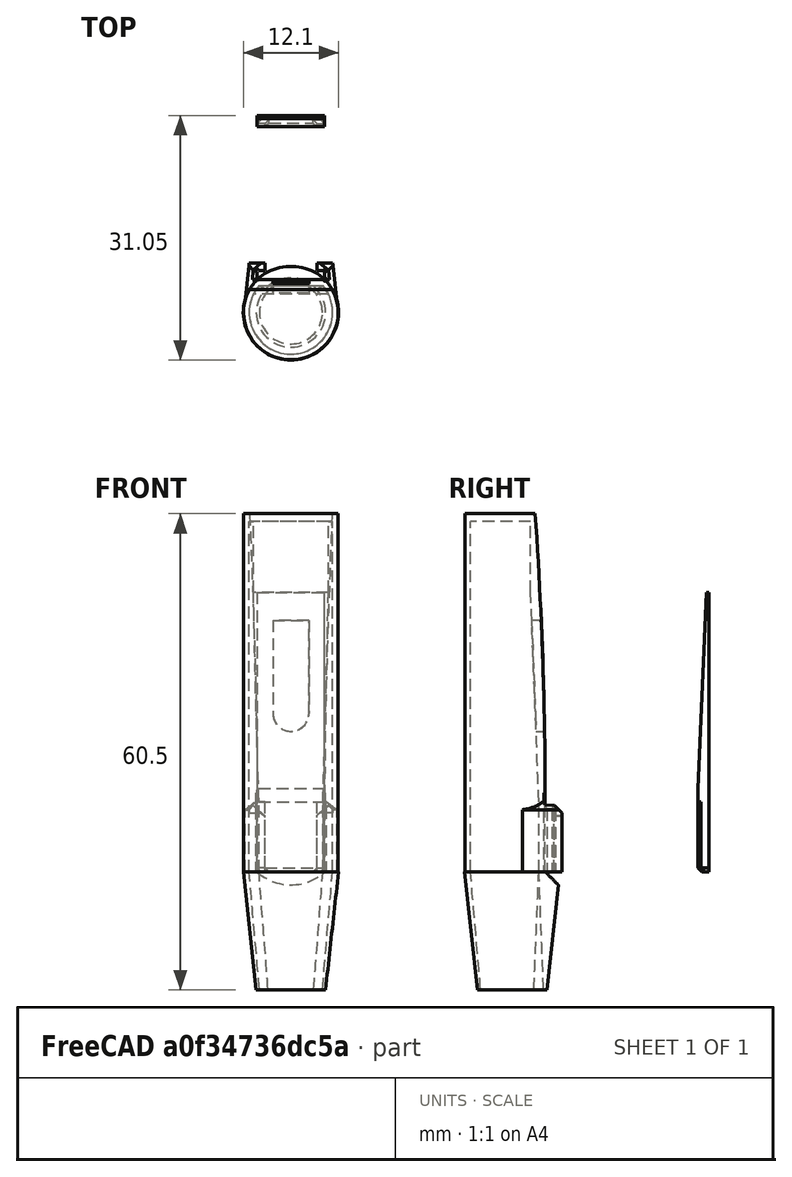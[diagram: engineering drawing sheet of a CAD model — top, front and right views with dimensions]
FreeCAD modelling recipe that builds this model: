
FCSTD DOCUMENT  (FreeCAD 1.0R38641 +678 (Git))
Label: stroik1-D-leaf_PLA
License: All rights reserved
LicenseURL: https://en.wikipedia.org/wiki/All_rights_reserved
objects: Sketcher::SketchObject×17, PartDesign::Pocket×10, PartDesign::Pad×4, PartDesign::Chamfer×3, App::VarSet×2, PartDesign::Body×2, Part::FeaturePython×1, PartDesign::FeatureBase×1, PartDesign::Mirrored×1, PartDesign::Plane×1, PartDesign::AdditiveLoft×1, PartDesign::ShapeBinder×1, Mesh::Feature×1
note: 97 computed .brp shape members not serialized (recipe doc carries the construction recipe); baked Part::Feature solids carry a one-line shape summary decoded from their .brp

FEATURE [Part::FeaturePython] Tube  # WARN: FeaturePython — macro-defined, semantics opaque (R4)
  AttacherType = Attacher::AttachEngine3D
  Height = 35.5
  InnerRadius = 5.3
  OuterRadius = 6
  Placement = pos=(0,0,0) rot=(0,1,0;1.5708rad)
  expr: Height = VarSet.leaf_len
  expr: InnerRadius = VarSet.d_inner
  expr: OuterRadius = VarSet.d_outer
FEATURE [PartDesign::FeatureBase] BaseFeature
  BaseFeature = -> Tube
  Suppressed = false
FEATURE [App::VarSet] VarSet
  d_inner = 5.3
  d_outer = 6
  d_outer_plug = 6.05
  leaf_end_thickness = 0.19
  leaf_gap = 1.85
  leaf_len = 35.5
  leaf_start_thickness = 1.42
  plug_inner_start = 4
  plug_len = 15
  plug_outer_start = 4.4
FEATURE [Sketcher::SketchObject] Sketch
  ArcFitTolerance = 1e-06
  AttachmentSupport = -> [YZ_Plane]
  ExternalGeometry = -> [BaseFeature]
  FullyConstrained = true
  MakeInternals = false
  MapMode = 5
  Placement = pos=(0,0,0) rot=(0.57735,0.57735,0.57735;2.0944rad)
  expr: Constraints[14] = VarSet.leaf_len / 4
  expr: Constraints[8] = VarSet.d_outer * 0.3
  sketch-geometry (6):
    g0: LineSegment StartX=6 StartY=35.5 StartZ=0 EndX=4.2 EndY=35.5 EndZ=0
    g1: LineSegment StartX=4.2 StartY=0 StartZ=0 EndX=6 EndY=0 EndZ=0
    g2: LineSegment StartX=6 StartY=0 StartZ=0 EndX=6 EndY=8.875 EndZ=0
    g3: LineSegment StartX=6 StartY=8.875 StartZ=0 EndX=6 EndY=35.5 EndZ=0
    g4: LineSegment StartX=4.2 StartY=35.5 StartZ=0 EndX=4.2 EndY=8.875 EndZ=0
    g5: LineSegment StartX=4.2 StartY=8.875 StartZ=0 EndX=4.2 EndY=0 EndZ=0
  constraints (17):
    c: Coincident(g0,g4)
    c: Coincident(g5,g1)
    c: Coincident(g1,g2)
    c: Coincident(g3,g0)
    c: Horizontal(g0)
    c: Horizontal(g1)
    c: Coincident(g0,g-3)
    c: PointOnObject(g5,g-4)
    c: DistanceX(g5,g1) = 1.8
    c: Coincident(g2,g3)
    c: Vertical(g2)
    c: Vertical(g3)
    c: Coincident(g4,g5)
    c: Vertical(g5)
    c: DistanceY(g2,g2) = 8.875
    c: Horizontal(g2,g4)
    c: Vertical(g4)
FEATURE [Sketcher::SketchObject] Sketch001
  ArcFitTolerance = 1e-06
  AttachmentSupport = -> [YZ_Plane]
  ExternalGeometry = -> [Sketch]
  FullyConstrained = true
  MakeInternals = false
  MapMode = 5
  Placement = pos=(0,0,0) rot=(0.57735,0.57735,0.57735;2.0944rad)
  expr: Constraints[12] = 0.8
  expr: Constraints[13] = VarSet.leaf_gap
  sketch-geometry (6):
    g0: LineSegment StartX=4.2 StartY=0 StartZ=0 EndX=3.4 EndY=0 EndZ=0
    g1: LineSegment StartX=3.4 StartY=0 StartZ=0 EndX=3.4 EndY=8.875 EndZ=0
    g2: LineSegment StartX=3.4 StartY=8.875 StartZ=0 EndX=2.35 EndY=35.5 EndZ=0
    g3: LineSegment StartX=2.35 StartY=35.5 StartZ=0 EndX=4.2 EndY=35.5 EndZ=0
    g4: LineSegment StartX=4.2 StartY=35.5 StartZ=0 EndX=4.2 EndY=8.875 EndZ=0
    g5: LineSegment StartX=4.2 StartY=8.875 StartZ=0 EndX=4.2 EndY=0 EndZ=0
  constraints (15):
    c: Coincident(g-4,g0)
    c: PointOnObject(g0,g-1)
    c: Coincident(g0,g1)
    c: Vertical(g1)
    c: Coincident(g1,g2)
    c: Coincident(g2,g3)
    c: Coincident(g3,g-3)
    c: Horizontal(g3)
    c: Coincident(g3,g4)
    c: Coincident(g4,g-4)
    c: Coincident(g4,g5)
    c: Coincident(g5,g0)
    c: DistanceX(g1,g4) = 0.8
    c: DistanceX(g2,g3) = 1.85
    c: Horizontal(g1,g4)
FEATURE [PartDesign::Pocket] Pocket  label="1 ścięcie"
  BaseFeature = -> BaseFeature
  Direction = (-1,0,0)
  Length = 5
  Length2 = 5
  Midplane = true
  Profile = -> Sketch
  ReferenceAxis = -> Sketch [N_Axis]
  Refine = true
  Suppressed = false
  Type = 1
FEATURE [PartDesign::Pad] Pad  label="uzupełnienie"
  AlongSketchNormal = false
  BaseFeature = -> Pocket
  Direction = (1,0,0)
  Length = 13
  Length2 = 10
  Midplane = true
  Profile = -> Sketch001
  ReferenceAxis = -> Sketch001 [N_Axis]
  Refine = true
  Suppressed = false
  Type = 1
  UpToShape = -> [Pocket]
FEATURE [PartDesign::Mirrored] Mirrored
  BaseFeature = -> Pad
  MirrorPlane = -> YZ_Plane
  Originals = -> [Pad]
  Refine = true
  Suppressed = false
  TransformMode = 0
FEATURE [Sketcher::SketchObject] Sketch002
  ArcFitTolerance = 1e-06
  AttachmentSupport = -> [Mirrored]
  ExternalGeometry = -> [Mirrored]
  FullyConstrained = true
  MakeInternals = false
  MapMode = 5
  Placement = pos=(0,4.2,0) rot=(0,0.707107,0.707107;3.14159rad)
  expr: Constraints[11] = VarSet.d_outer / 3
  expr: Constraints[8] = VarSet.leaf_len / 10
  expr: Constraints[9] = VarSet.leaf_len / 3
  sketch-geometry (4):
    g0: LineSegment StartX=2.28486 StartY=20.1167 StartZ=0 EndX=2.28486 EndY=31.95 EndZ=0
    g1: LineSegment StartX=2.28486 StartY=31.95 StartZ=0 EndX=-2.28486 EndY=31.95 EndZ=0
    g2: LineSegment StartX=-2.28486 StartY=31.95 StartZ=0 EndX=-2.28486 EndY=20.1167 EndZ=0
    g3: ArcOfCircle CenterX=0 CenterY=20.1167 CenterZ=0 NormalX=0 NormalY=0 NormalZ=1 AngleXU=0 Radius=2.28486 StartAngle=3.14159 EndAngle=6.28319
  constraints (12):
    c: Coincident(g0,g1)
    c: Coincident(g1,g2)
    c: Coincident(g3,g2)
    c: Coincident(g3,g0)
    c: PointOnObject(g3,g-2)
    c: Horizontal(g0,g2)
    c: Horizontal(g2,g3)
    c: Symmetric(g0,g1,g-2)
    c: DistanceY(g1,g-7) = 3.55
    c: DistanceY(g3,g1) = 11.8333
    c: Vertical(g1,g2)
    c: DistanceX(g0,g-6) = 2
FEATURE [PartDesign::Pocket] Pocket001  label="dziurka"
  BaseFeature = -> Mirrored
  Direction = (0,-1,2e-16)
  Length = 2.65
  Length2 = 5
  Profile = -> Sketch002
  ReferenceAxis = -> Sketch002 [N_Axis]
  Refine = true
  Suppressed = false
  Type = 0
  expr: Length = VarSet.d_inner / 2
FEATURE [Sketcher::SketchObject] Sketch003
  ArcFitTolerance = 1e-06
  AttachmentSupport = -> [Pocket001]
  ExternalGeometry = -> [Pocket001]
  FullyConstrained = true
  MakeInternals = false
  MapMode = 5
  Placement = pos=(0,0,35.5) rot=(0,0,1;0rad)
  sketch-geometry (2):
    g0: ArcOfCircle CenterX=0 CenterY=0 CenterZ=0 NormalX=0 NormalY=0 NormalZ=1 AngleXU=0 Radius=6 StartAngle=2.3662 EndAngle=7.05858
    g1: LineSegment StartX=-4.28486 StartY=4.2 StartZ=0 EndX=4.28486 EndY=4.2 EndZ=0
  constraints (5):
    c: Coincident(g0,g-1)
    c: Coincident(g0,g-4)
    c: Coincident(g1,g0)
    c: Coincident(g1,g0)
    c: Horizontal(g1)
FEATURE [PartDesign::Pad] Pad001  label="zaślepka"
  BaseFeature = -> Pocket001
  Direction = (0,0,1)
  Length = 10
  Length2 = 10
  Profile = -> Sketch003
  ReferenceAxis = -> Sketch003 [N_Axis]
  Refine = true
  Suppressed = false
  Type = 0
FEATURE [Sketcher::SketchObject] Sketch004
  ArcFitTolerance = 1e-06
  AttachmentSupport = -> [Pad001]
  ExternalGeometry = -> [Pad001]
  FullyConstrained = true
  MakeInternals = false
  MapMode = 5
  Placement = pos=(0,0,0) rot=(1,0,0;3.14159rad)
  expr: Constraints[4] = VarSet.d_outer_plug
  expr: Constraints[7] = VarSet.d_inner
  sketch-geometry (3):
    g0: ArcOfCircle CenterX=0 CenterY=0 CenterZ=0 NormalX=0 NormalY=0 NormalZ=1 AngleXU=0 Radius=5.3 StartAngle=5.58672 EndAngle=10.1212
    g1: LineSegment StartX=-4.06571 StartY=-3.4 StartZ=0 EndX=4.06571 EndY=-3.4 EndZ=0
    g2: Circle CenterX=0 CenterY=0 CenterZ=0 NormalX=0 NormalY=0 NormalZ=1 AngleXU=0 Radius=6.05
  constraints (8):
    c: Coincident(g1,g0)
    c: Horizontal(g1)
    c: Coincident(g2,g0)
    c: Coincident(g-1,g0)
    c: Radius(g2) = 6.05
    c: Horizontal(g0,g-6)
    c: Coincident(g1,g0)
    c: Radius(g0) = 5.3
FEATURE [PartDesign::Plane] DatumPlane
  AttachmentOffset = pos=(0,0,15) rot=(0,0,1;0rad)
  AttachmentSupport = -> [Pocket001]
  Length = 60
  MapMode = 5
  Placement = pos=(0,0,-15) rot=(1,0,0;3.14159rad)
  ResizeMode = 0
  Width = 60
  expr: .AttachmentOffset.Base.z = VarSet.plug_len
FEATURE [Sketcher::SketchObject] Sketch005
  ArcFitTolerance = 1e-06
  AttachmentSupport = -> [DatumPlane]
  ExternalGeometry = -> [Sketch004,Pad001]
  FullyConstrained = true
  MakeInternals = false
  MapMode = 5
  Placement = pos=(0,0,-15) rot=(1,0,0;3.14159rad)
  expr: Constraints[2] = VarSet.plug_inner_start
  expr: Constraints[3] = VarSet.plug_outer_start
  sketch-geometry (2):
    g0: Circle CenterX=0 CenterY=0 CenterZ=0 NormalX=0 NormalY=0 NormalZ=1 AngleXU=0 Radius=4
    g1: Circle CenterX=0 CenterY=0 CenterZ=0 NormalX=0 NormalY=0 NormalZ=1 AngleXU=0 Radius=4.4
  constraints (4):
    c: Coincident(g0,g-1)
    c: Coincident(g1,g0)
    c: Radius(g0) = 4
    c: Radius(g1) = 4.4
FEATURE [PartDesign::AdditiveLoft] AdditiveLoft  label="dziubek"
  BaseFeature = -> Pad001
  Closed = false
  Profile = -> Sketch005
  Refine = true
  Ruled = false
  Sections = -> [Sketch004]
  Suppressed = false
FEATURE [Sketcher::SketchObject] Sketch006
  ArcFitTolerance = 1e-06
  AttachmentSupport = -> [Pad001]
  ExternalGeometry = -> [Pad001]
  FullyConstrained = false
  MakeInternals = false
  MapMode = 5
  Placement = pos=(0,0,0) rot=(1,0,0;3.14159rad)
  expr: Constraints[24] = 1.1 mm
  sketch-geometry (16):
    g0: LineSegment StartX=4.28486 StartY=-4.2 StartZ=0 EndX=6 EndY=0 EndZ=0
    g1: LineSegment StartX=6 StartY=0 StartZ=0 EndX=5.28986 EndY=-6.3 EndZ=0
    g2: LineSegment StartX=5.28986 StartY=-6.3 StartZ=0 EndX=3.28986 EndY=-6.3 EndZ=0
    g3: LineSegment StartX=3.28986 StartY=-6.3 StartZ=0 EndX=3.28986 EndY=-5.3 EndZ=0
    g4: LineSegment StartX=3.28986 StartY=-5.3 StartZ=0 EndX=4.28986 EndY=-5.3 EndZ=0
    g5: LineSegment StartX=-5.28986 StartY=-6.3 StartZ=0 EndX=-3.28986 EndY=-6.3 EndZ=0
    g6: LineSegment StartX=-6 StartY=0 StartZ=0 EndX=-5.28986 EndY=-6.3 EndZ=0
    g7: LineSegment StartX=-4.28486 StartY=-4.2 StartZ=0 EndX=-6 EndY=0 EndZ=0
    g8: LineSegment StartX=-3.28986 StartY=-5.3 StartZ=0 EndX=-4.28986 EndY=-5.3 EndZ=0
    g9: LineSegment StartX=-3.28986 StartY=-6.3 StartZ=0 EndX=-3.28986 EndY=-5.3 EndZ=0
    g10: LineSegment StartX=4.28986 StartY=-5.3 StartZ=0 EndX=4.28986 EndY=-4.2 EndZ=0
    g11: LineSegment StartX=-4.28986 StartY=-5.3 StartZ=0 EndX=-4.28986 EndY=-4.2 EndZ=0
    g12: LineSegment StartX=4.28986 StartY=-4.2 StartZ=0 EndX=4.28717 EndY=-4.19654 EndZ=0
    g13: LineSegment StartX=4.28717 StartY=-4.19654 StartZ=0 EndX=4.28486 EndY=-4.2 EndZ=0
    g14: LineSegment StartX=-4.28986 StartY=-4.2 StartZ=0 EndX=-4.28627 EndY=-4.19642 EndZ=0
    g15: LineSegment StartX=-4.28627 StartY=-4.19642 StartZ=0 EndX=-4.28486 EndY=-4.2 EndZ=0
  constraints (36):
    c: Coincident(g-5,g0)
    c: Coincident(g0,g1)
    c: Coincident(g1,g2)
    c: Horizontal(g2)
    c: Coincident(g2,g3)
    c: Vertical(g3)
    c: Coincident(g3,g4)
    c: Horizontal(g4)
    c: Coincident(g4,g10)
    c: Coincident(g13,g0)
    c: Coincident(g7,g6)
    c: Coincident(g6,g5)
    c: Coincident(g5,g9)
    c: Vertical(g9)
    c: Coincident(g9,g8)
    c: Horizontal(g8)
    c: Coincident(g8,g11)
    c: Coincident(g15,g7)
    c: Symmetric(g2,g5,g-2)
    c: DistanceX(g4,g4) = 1
    c: Symmetric(g4,g11,g-2)
    c: Symmetric(g0,g6,g-2)
    c: DistanceY(g3,g3) = 1
    c: Symmetric(g7,g0,g-2)
    c: DistanceY(g10,g13) = 1.1
    c: DistanceX(g2,g2) = 2
    c: Coincident(g0,g-5)
    c: Symmetric(g5,g1,g-2)
    c: Coincident(g10,g12)
    c: Vertical(g10)
    c: Horizontal(g10,g0)
    c: DistanceX(g13,g12) = 0.005
    c: Coincident(g11,g14)
    c: Symmetric(g11,g10,g-2)
    c: Coincident(g12,g13)
    c: Coincident(g14,g15)
FEATURE [PartDesign::Pad] Pad002  label="uchwyt na listek"
  BaseFeature = -> AdditiveLoft
  Direction = (0,0,-1)
  Length = 8.875
  Length2 = 10
  Profile = -> Sketch006
  ReferenceAxis = -> Sketch006 [N_Axis]
  Refine = true
  Reversed = true
  Suppressed = false
  Type = 0
  expr: Length = VarSet.leaf_len / 4
FEATURE [Sketcher::SketchObject] Sketch009
  ArcFitTolerance = 1e-06
  AttachmentSupport = -> [YZ_Plane]
  ExternalGeometry = -> [Pad001]
  FullyConstrained = false
  MakeInternals = false
  MapMode = 5
  Placement = pos=(0,0,0) rot=(0.57735,0.57735,0.57735;2.0944rad)
  expr: .Constraints.gap = VarSet.leaf_gap
  expr: Constraints[19] = 3 / 4 * VarSet.leaf_len * 2 / 2
  expr: Constraints[1] = VarSet.leaf_len / 4
  expr: Constraints[20] = 3 / 4 * VarSet.leaf_len * 2
  sketch-geometry (13):
    g0: GeomPoint X=4.2 Y=8.875 Z=0
    g1: Circle [constr] CenterX=4.2 CenterY=8.875 CenterZ=0 NormalX=0 NormalY=0 NormalZ=1 AngleXU=0 Radius=1
    g2: Circle [constr] CenterX=4.2 CenterY=35.5 CenterZ=0 NormalX=0 NormalY=0 NormalZ=1 AngleXU=0 Radius=1
    g3: Circle [constr] CenterX=1.51024 CenterY=62.125 CenterZ=0 NormalX=0 NormalY=0 NormalZ=1 AngleXU=0 Radius=1
    g4: BSplineCurve PolesCount=3 KnotsCount=2 Degree=2 IsPeriodic=0
    g5: GeomPoint [constr] X=4.2 Y=8.875 Z=0
    g6: GeomPoint [constr] X=1.51024 Y=62.125 Z=0
    g7: LineSegment [constr] StartX=1.51024 StartY=62.125 StartZ=0 EndX=4.2 EndY=8.875 EndZ=0
    g8: LineSegment StartX=104.2 StartY=41.25 StartZ=0 EndX=104.2 EndY=8.875 EndZ=0
    g9: LineSegment StartX=104.2 StartY=8.875 StartZ=0 EndX=4.2 EndY=8.875 EndZ=0
    g10: LineSegment StartX=1.51024 StartY=62.125 StartZ=0 EndX=1.51024 EndY=90 EndZ=0
    g11: LineSegment StartX=1.51024 StartY=90 StartZ=0 EndX=104.2 EndY=41.25 EndZ=0
    g12: LineSegment [constr] StartX=4.2 StartY=45.5 StartZ=0 EndX=2.35 EndY=45.5 EndZ=0
  constraints (29):
    c: PointOnObject(g0,g-3)
    c: DistanceY(g-3,g0) = 8.875
    c: Weight(g1) = 1
    c: Equal(g1,g2)
    c: Equal(g1,g3)
    c: InternalAlignment(g1,g4)
    c: InternalAlignment(g2,g4)
    c: InternalAlignment(g3,g4)
    c: InternalAlignment(g5,g4)
    c: InternalAlignment(g6,g4)
    c: Coincident(g1,g0)
    c: Coincident(g7,g4)
    c: Coincident(g7,g4)
    c: Vertical(g8)
    c: Coincident(g8,g9)
    c: Coincident(g9,g0)
    c: Horizontal(g9)
    c: DistanceX(g9,g9) = 100
    c: Vertical(g-3,g2)
    c: DistanceY(g0,g2) = 26.625
    c: DistanceY(g0,g4) = 53.25
    c: Coincident(g10,g4)
    c: Vertical(g10)
    c: Coincident(g11,g10)
    c: Coincident(g11,g8)
    c: Coincident(g12,g-3)
    c: PointOnObject(g12,g7)
    c: Horizontal(g12)
    c: DistanceX(g12,g12) = 1.85  'gap'
FEATURE [PartDesign::Pocket] Pocket003  label="2 ścięcie"
  BaseFeature = -> Pad002
  Direction = (-1,0,0)
  Length = 100
  Length2 = 5
  Midplane = true
  Profile = -> Sketch009
  ReferenceAxis = -> Sketch009 [N_Axis]
  Refine = true
  Suppressed = false
  Type = 0
FEATURE [PartDesign::ShapeBinder] ShapeBinder
  Support = -> [Mirrored]
  TraceSupport = false
FEATURE [Sketcher::SketchObject] Sketch010  label="main shape"
  ArcFitTolerance = 1e-06
  AttachmentSupport = -> [XZ_Plane001]
  ExternalGeometry = -> [ShapeBinder]
  FullyConstrained = true
  MakeInternals = false
  MapMode = 5
  Placement = pos=(0,0,0) rot=(1,0,0;1.5708rad)
  expr: Constraints[6] = VarSet.leaf_len / 4
  expr: Constraints[9] = VarSet.leaf_len
  sketch-geometry (6):
    g0: LineSegment StartX=-4.28486 StartY=0 StartZ=0 EndX=4.28486 EndY=9e-16 EndZ=0
    g1: LineSegment StartX=4.28486 StartY=9e-16 StartZ=0 EndX=4.28486 EndY=8.875 EndZ=0
    g2: LineSegment StartX=-4.28486 StartY=8.875 StartZ=0 EndX=-4.28486 EndY=0 EndZ=0
    g3: LineSegment StartX=4.28486 StartY=8.875 StartZ=0 EndX=4.28486 EndY=35.5 EndZ=0
    g4: LineSegment StartX=-4.28486 StartY=8.875 StartZ=0 EndX=-4.28486 EndY=35.5 EndZ=0
    g5: LineSegment StartX=-4.28486 StartY=35.5 StartZ=0 EndX=4.28486 EndY=35.5 EndZ=0
  constraints (15):
    c: Coincident(g0,g1)
    c: Coincident(g2,g0)
    c: Vertical(g1)
    c: Vertical(g2)
    c: Coincident(g0,g-3)
    c: Coincident(g0,g-3)
    c: DistanceY(g1,g1) = 8.875
    c: Coincident(g3,g1)
    c: Symmetric(g3,g4,g-2)
    c: DistanceY(g0,g3) = 35.5
    c: Horizontal(g2,g1)
    c: Coincident(g4,g2)
    c: Coincident(g5,g4)
    c: Coincident(g5,g3)
    c: Vertical(g3)
FEATURE [PartDesign::Pad] Pad003
  Direction = (0,-1,2e-16)
  Length = 1.42
  Length2 = 10
  Placement = pos=(0,0,0) rot=(1,0,0;1.5708rad)
  Profile = -> Sketch010
  ReferenceAxis = -> Sketch010 [N_Axis]
  Refine = true
  Suppressed = false
  Type = 0
  expr: Length = VarSet.leaf_start_thickness
FEATURE [Sketcher::SketchObject] Sketch011
  ArcFitTolerance = 1e-06
  AttachmentSupport = -> [Pad003]
  ExternalGeometry = -> [Pad003]
  FullyConstrained = true
  MakeInternals = false
  MapMode = 5
  Placement = pos=(0,0,5e-16) rot=(1,0,0;3.14159rad)
  sketch-geometry (8):
    g0: LineSegment StartX=-3.28486 StartY=1.42 StartZ=0 EndX=-3.28486 EndY=1 EndZ=0
    g1: LineSegment StartX=-3.28486 StartY=1 StartZ=0 EndX=-8.28486 EndY=1 EndZ=0
    g2: LineSegment StartX=-8.28486 StartY=1 StartZ=0 EndX=-8.28486 EndY=4.92104 EndZ=0
    g3: LineSegment StartX=-8.28486 StartY=4.92104 StartZ=0 EndX=-3.28486 EndY=1.42 EndZ=0
    g4: LineSegment StartX=8.28486 StartY=4.92104 StartZ=0 EndX=3.28486 EndY=1.42 EndZ=0
    g5: LineSegment StartX=3.28486 StartY=1.42 StartZ=0 EndX=3.28486 EndY=1 EndZ=0
    g6: LineSegment StartX=3.28486 StartY=1 StartZ=0 EndX=8.28486 EndY=1 EndZ=0
    g7: LineSegment StartX=8.28486 StartY=1 StartZ=0 EndX=8.28486 EndY=4.92104 EndZ=0
  constraints (21):
    c: PointOnObject(g0,g-3)
    c: Vertical(g0)
    c: Coincident(g0,g1)
    c: Horizontal(g1)
    c: Coincident(g1,g2)
    c: Vertical(g2)
    c: Coincident(g2,g3)
    c: Coincident(g3,g0)
    c: DistanceX(g-4,g0) = 1
    c: Vertical(g5)
    c: Coincident(g5,g6)
    c: Coincident(g6,g7)
    c: Coincident(g7,g4)
    c: Coincident(g4,g5)
    c: Symmetric(g4,g0,g-2)
    c: Symmetric(g5,g0,g-2)
    c: Symmetric(g6,g1,g-2)
    c: Symmetric(g4,g2,g-2)
    c: DistanceY(g-5,g0) = 1
    c: Angle(g-3,g3) = 2.53073
    c: DistanceX(g1,g1) = 5
FEATURE [PartDesign::Pocket] Pocket004  label="uchwyt"
  BaseFeature = -> Pad003
  Direction = (0,0,1)
  Length = 8.875
  Length2 = 5
  Placement = pos=(0,0,0) rot=(1,0,0;1.5708rad)
  Profile = -> Sketch011
  ReferenceAxis = -> Sketch011 [N_Axis]
  Refine = true
  Suppressed = false
  Type = 0
  expr: Length = VarSet.leaf_len / 4
FEATURE [Sketcher::SketchObject] Sketch012
  ArcFitTolerance = 1e-06
  AttachmentSupport = -> [Pocket004]
  FullyConstrained = true
  MakeInternals = false
  MapMode = 5
  Placement = pos=(-4.28486,0,-3.06e-14) rot=(0.707107,0,-0.707107;3.14159rad)
  expr: Constraints[0] = VarSet.d_inner + 0.4 mm
  expr: Constraints[5] = VarSet.leaf_end_thickness
  sketch-geometry (3):
    g0: LineSegment StartX=-39.052 StartY=0.19 StartZ=0 EndX=-10.0388 EndY=1.44 EndZ=0
    g1: LineSegment StartX=-39.052 StartY=0.19 StartZ=0 EndX=-39.052 EndY=14.02 EndZ=0
    g2: LineSegment StartX=-39.052 StartY=14.02 StartZ=0 EndX=-10.0388 EndY=1.44 EndZ=0
  constraints (8):
    c: DistanceX(g0,g-3) = 5.7
    c: Coincident(g1,g0)
    c: Vertical(g1)
    c: Coincident(g2,g1)
    c: Coincident(g2,g0)
    c: DistanceY(g-4,g0) = 0.19
    c: Coincident(g0,g-3)
    c: DistanceY(g1,g1) = 13.83
FEATURE [PartDesign::Pocket] Pocket005  label="Pochylenie"
  BaseFeature = -> Pocket004
  Direction = (1,0,7.1e-15)
  Length = 5
  Length2 = 5
  Placement = pos=(0,0,0) rot=(1,0,0;1.5708rad)
  Profile = -> Sketch012
  ReferenceAxis = -> Sketch012 [N_Axis]
  Refine = true
  Suppressed = false
  Type = 1
FEATURE [PartDesign::Chamfer] Chamfer
  Angle = 45
  Base = -> Pocket003 [?Edge89,?Edge77]
  BaseFeature = -> Pocket003
  ChamferType = 0
  FlipDirection = false
  Refine = true
  Size = 2
  Size2 = 1
  SupportTransform = false
  Suppressed = true
  UseAllEdges = false
FEATURE [Sketcher::SketchObject] Sketch013
  ArcFitTolerance = 1e-06
  AttachmentSupport = -> [YZ_Plane]
  FullyConstrained = true
  MakeInternals = false
  MapMode = 5
  Placement = pos=(0,0,0) rot=(0.57735,0.57735,0.57735;2.0944rad)
  sketch-geometry (3):
    g0: LineSegment StartX=4.2 StartY=0 StartZ=0 EndX=18.3421 EndY=-14.1421 EndZ=0
    g1: LineSegment StartX=18.3421 StartY=-14.1421 StartZ=0 EndX=18.3421 EndY=1.8e-15 EndZ=0
    g2: LineSegment StartX=18.3421 StartY=1.8e-15 StartZ=0 EndX=4.2 EndY=0 EndZ=0
  constraints (8):
    c: Coincident(g-3,g0)
    c: Coincident(g0,g1)
    c: Vertical(g1)
    c: Coincident(g1,g2)
    c: Coincident(g2,g0)
    c: Angle(g-2,g0) = 0.785398
    c: Distance(g0,g0) = 20
    c: Angle(g0,g2) = 0.785398
FEATURE [PartDesign::Pocket] Pocket006
  BaseFeature = -> Chamfer
  Direction = (-1,0,0)
  Length = 5
  Length2 = 5
  Midplane = true
  Profile = -> Sketch013
  ReferenceAxis = -> Sketch013 [N_Axis]
  Refine = true
  Suppressed = false
  Type = 1
FEATURE [Sketcher::SketchObject] Sketch014
  ArcFitTolerance = 1e-06
  AttachmentSupport = -> [Pocket006]
  ExternalGeometry = -> [Mirrored]
  FullyConstrained = true
  MakeInternals = false
  MapMode = 5
  Placement = pos=(0,0,35.5) rot=(1,0,0;3.14159rad)
  sketch-geometry (2):
    g0: ArcOfCircle CenterX=0 CenterY=0 CenterZ=0 NormalX=0 NormalY=0 NormalZ=1 AngleXU=0 Radius=5.3 StartAngle=5.8238 EndAngle=9.88416
    g1: LineSegment StartX=4.75053 StartY=-2.35 StartZ=0 EndX=-4.75053 EndY=-2.35 EndZ=0
  constraints (5):
    c: Coincident(g0,g-1)
    c: Coincident(g0,g-4)
    c: Coincident(g1,g0)
    c: Coincident(g1,g0)
    c: Horizontal(g1)
FEATURE [PartDesign::Pocket] Pocket007
  BaseFeature = -> Pocket006
  Direction = (0,0,1)
  Length = 9
  Length2 = 5
  Profile = -> Sketch014
  ReferenceAxis = -> Sketch014 [N_Axis]
  Refine = true
  Suppressed = false
  Type = 0
FEATURE [App::VarSet] VarSet001  label="VarSet009"
  d_inner = 5.3
  d_outer = 6
  d_outer_plug = 6
  leaf_angle = 0
  leaf_angle2 = 1.6
  leaf_end_thickness = 0.2
  leaf_len = 39
  leaf_start_thickness = 1.45
  plug_inner_start = 4
  plug_len = 15
  plug_outer_start = 4.4
FEATURE [Sketcher::SketchObject] Sketch015
  ArcFitTolerance = 1e-06
  AttachmentSupport = -> [Pocket007]
  FullyConstrained = true
  MakeInternals = false
  MapMode = 5
  Placement = pos=(0,6.3,0) rot=(0,0.707107,0.707107;3.14159rad)
FEATURE [Sketcher::SketchObject] Sketch016
  ArcFitTolerance = 1e-06
  AttachmentSupport = -> [Pocket007]
  ExternalGeometry = -> [Pocket007]
  FullyConstrained = false
  MakeInternals = false
  MapMode = 5
  Placement = pos=(0,6.3,0) rot=(0,0.707107,0.707107;3.14159rad)
  sketch-geometry (6):
    g0: LineSegment StartX=-5.28986 StartY=8.875 StartZ=0 EndX=-2.018 EndY=6.06813 EndZ=0
    g1: LineSegment StartX=-2.018 StartY=6.06813 StartZ=0 EndX=-2.018 EndY=11.9722 EndZ=0
    g2: LineSegment StartX=-2.018 StartY=11.9722 StartZ=0 EndX=-5.28986 EndY=8.875 EndZ=0
    g3: LineSegment StartX=5.28986 StartY=8.875 StartZ=0 EndX=2.26844 EndY=6.06813 EndZ=0
    g4: LineSegment StartX=2.26844 StartY=6.06813 StartZ=0 EndX=2.26844 EndY=11.9722 EndZ=0
    g5: LineSegment StartX=2.26844 StartY=11.9722 StartZ=0 EndX=5.28986 EndY=8.875 EndZ=0
  constraints (12):
    c: Coincident(g-3,g0)
    c: Coincident(g0,g1)
    c: Vertical(g1)
    c: Coincident(g1,g2)
    c: Coincident(g2,g0)
    c: Coincident(g-4,g3)
    c: Coincident(g3,g4)
    c: Vertical(g4)
    c: Coincident(g4,g5)
    c: Coincident(g5,g3)
    c: Horizontal(g0,g3)
    c: Horizontal(g1,g4)
FEATURE [PartDesign::Pocket] Pocket008
  BaseFeature = -> Pocket007
  Direction = (0,-1,2e-16)
  Length = 2.1
  Length2 = 5
  Profile = -> Sketch016
  ReferenceAxis = -> Sketch016 [N_Axis]
  Refine = true
  Suppressed = false
  Type = 0
FEATURE [Sketcher::SketchObject] Sketch017
  ArcFitTolerance = 1e-06
  AttachmentSupport = -> [Pocket008]
  FullyConstrained = false
  MakeInternals = false
  MapMode = 5
  Placement = pos=(4.28986,0,0) rot=(0.57735,-0.57735,-0.57735;2.0944rad)
  sketch-geometry (3):
    g0: LineSegment StartX=-4.21102 StartY=9.75787 StartZ=0 EndX=-7.69576 EndY=5.94234 EndZ=0
    g1: LineSegment StartX=-7.69576 StartY=5.94234 StartZ=0 EndX=-7.9348 EndY=11.8707 EndZ=0
    g2: LineSegment StartX=-7.9348 StartY=11.8707 StartZ=0 EndX=-4.21102 EndY=9.75787 EndZ=0
  constraints (3):
    c: Coincident(g0,g1)
    c: Coincident(g1,g2)
    c: Coincident(g2,g0)
FEATURE [PartDesign::Pocket] Pocket009
  BaseFeature = -> Pocket008
  Direction = (1,0,0)
  Length = 5
  Length2 = 5
  Midplane = true
  Profile = -> Sketch017
  ReferenceAxis = -> Sketch017 [N_Axis]
  Refine = true
  Suppressed = false
  Type = 1
FEATURE [PartDesign::Chamfer] Chamfer001
  Angle = 45
  Base = -> Pocket009 [Edge63,Edge81]
  BaseFeature = -> Pocket009
  ChamferType = 0
  FlipDirection = false
  Refine = true
  Size = 1
  Size2 = 1
  SupportTransform = false
  Suppressed = false
  UseAllEdges = false
FEATURE [Sketcher::SketchObject] Sketch018
  ArcFitTolerance = 1e-06
  AttachmentSupport = -> [Chamfer001]
  FullyConstrained = false
  MakeInternals = false
  MapMode = 5
  Placement = pos=(0,0,0) rot=(1,0,0;3.14159rad)
  sketch-geometry (4):
    g0: Circle CenterX=4.28986 CenterY=-4.2 CenterZ=0 NormalX=0 NormalY=0 NormalZ=1 AngleXU=0 Radius=0.2
    g1: Circle CenterX=-4.28986 CenterY=-4.2 CenterZ=0 NormalX=0 NormalY=0 NormalZ=1 AngleXU=0 Radius=0.2
    g2: Circle CenterX=-4.28986 CenterY=-5.3 CenterZ=0 NormalX=0 NormalY=0 NormalZ=1 AngleXU=0 Radius=0.19996
    g3: Circle CenterX=4.28986 CenterY=-5.24596 CenterZ=0 NormalX=0 NormalY=0 NormalZ=1 AngleXU=0 Radius=0.197638
  constraints (6):
    c: Coincident(g0,g-4)
    c: Diameter(g0) = 0.4
    c: Coincident(g1,g-3)
    c: Diameter(g1) = 0.4
    c: Coincident(g2,g-3)
    c: Coincident(g3,g-4)
FEATURE [PartDesign::Pocket] Pocket010
  BaseFeature = -> Chamfer001
  Direction = (0,0,1)
  Length = 10
  Length2 = 5
  Profile = -> Sketch018
  ReferenceAxis = -> Sketch018 [N_Axis]
  Refine = true
  Suppressed = false
  Type = 0
FEATURE [PartDesign::Body] Body  label="stroik"
  AllowCompound = false
  BaseFeature = -> Tube
  Group = -> [BaseFeature,Sketch,Pocket,Sketch001,Pad,Mirrored,Sketch002,Pocket001,Sketch003,Pad001,Sketch004,DatumPlane,Sketch005,AdditiveLoft,Sketch006,Pad002,Sketch009,Pocket003,Chamfer,Sketch013,Pocket006,Sketch014,Pocket007,Sketch015,Sketch016,Pocket008,Sketch017,Pocket009,Chamfer001,Sketch018,Pocket010]
  Origin = -> Origin
  Tip = -> Pocket010
FEATURE [PartDesign::Chamfer] Chamfer002
  Angle = 45
  Base = -> Pocket005 [Edge7,Edge6,Edge5,Edge4,Edge3,Edge8,Edge2]
  BaseFeature = -> Pocket005
  ChamferType = 0
  FlipDirection = false
  Placement = pos=(0,0,0) rot=(1,0,0;1.5708rad)
  Refine = true
  Size = 0.5
  Size2 = 1
  SupportTransform = false
  Suppressed = false
  UseAllEdges = false
FEATURE [PartDesign::Body] Body001  label="listek"
  AllowCompound = false
  Group = -> [ShapeBinder,Sketch010,Pad003,Sketch011,Pocket004,Sketch012,Pocket005,Chamfer002]
  Origin = -> Origin001
  Placement = pos=(0,25,0) rot=(0,0,1;0rad)
  Tip = -> Chamfer002
FEATURE [Mesh::Feature] Mesh001  label="stroik (Meshed)"
